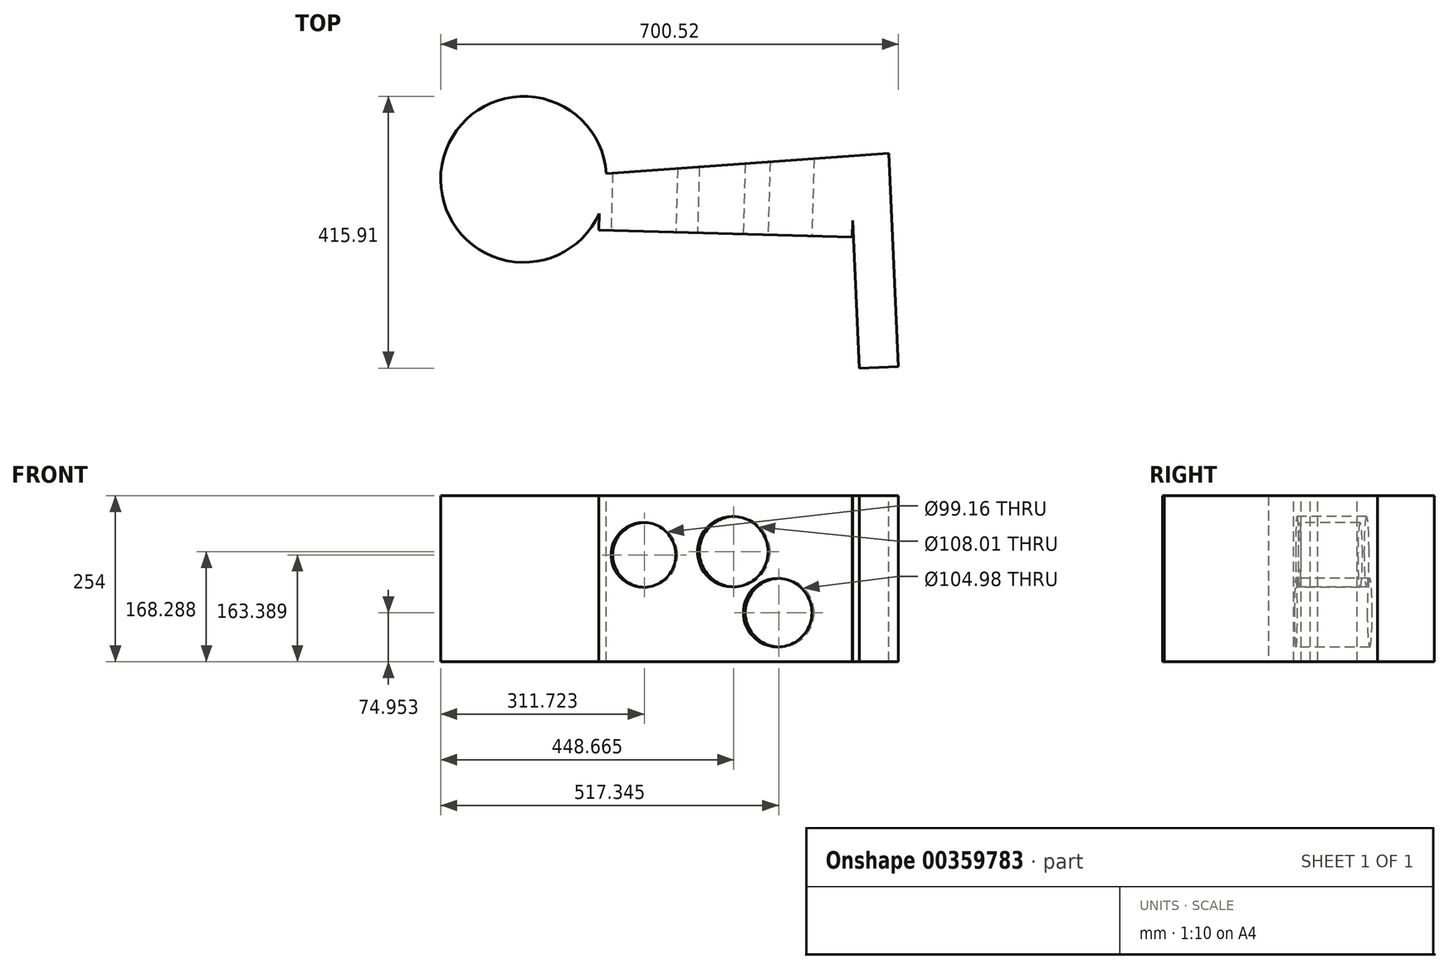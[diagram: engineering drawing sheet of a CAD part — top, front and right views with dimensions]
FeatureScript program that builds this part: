
annotation { "Feature Type Name" : "Feature", "Feature Type Description" : "" }
export const myFeature = defineFeature(function(context is Context, id is Id, definition is map)
    precondition{}
    {
        {
            var Q0;
            Q0=qCreatedBy(makeId("Top.planeOp"),FACE);
            var sketch = newSketch(context, id + "F0", { "sketchPlane" : qUnion([Q0])});
            skCircle(sketch, "E0", {"center": v(0, 0) * mm, "radius": 127 * mm});
            skSolve(sketch);
        }
        {
            var Q0;
            Q0=makeQuery(id+"F0.imprint","IMPRINT",FACE,{"disambiguationData":[TD([[makeQuery(id+"F0.imprint","IMPRINT",EDGE,{"derivedFrom":sQuery(id+"F0.wireOp",EDGE,"E0")}),1.0]])]});
            extrude(context, id + "F1", {"entities" : qUnion([Q0]), "depth" : 254 * mm});
        }
        {
            var Q0;
            Q0=makeQuery(id+"F1.opExtrude","CAP_FACE",FACE,{"disambiguationData":[OSD([sQuery(id+"F0.wireOp",EDGE,"E0")])],"isStart":false});
            var sketch = newSketch(context, id + "F2", { "sketchPlane" : qUnion([Q0])});
            skLineSegment(sketch, "E1", {"start": v(0, 0) * mm, "end": v(559.2, 39.98) * mm});
            skLineSegment(sketch, "E2", {"start": v(559.2, 39.98) * mm, "end": v(573.52, -286.29) * mm});
            skLineSegment(sketch, "E3", {"start": v(573.52, -286.29) * mm, "end": v(513.78, -288.91) * mm});
            skLineSegment(sketch, "E4", {"start": v(513.78, -288.91) * mm, "end": v(503.86, -62.83) * mm});
            skLineSegment(sketch, "E5", {"start": v(503.86, -62.83) * mm, "end": v(115.93, -51.87) * mm});
            skSolve(sketch);
        }
        {
            var Q0;
            {var subQ0=sQuery(id+"F2.wireOp",EDGE,"E2");Q0=makeQuery(id+"F2.imprint","IMPRINT",FACE,{"disambiguationData":[TD([[makeQuery(id+"F2.imprint","IMPRINT",EDGE,{"derivedFrom":subQ0}),-1.0]])]});}
            extrude(context, id + "F3", {"entities" : qUnion([Q0]), "operationType" : NewBodyOperationType.ADD, "oppositeDirection" : true, "depth" : 254 * mm});
        }
        {
            var Q0;
            Q0=makeQuery(id+"F3.opExtrude","SWEPT_FACE",FACE,{"disambiguationData":[OSD([sQuery(id+"F2.wireOp",EDGE,"E5")])]});
            extrude(context, id + "F4", {"entities" : qUnion([Q0]), "operationType" : NewBodyOperationType.ADD, "depth" : 25.4 * mm});
        }
        {
            var Q0;
            Q0=makeQuery(id+"F4.opExtrude","CAP_FACE",FACE,{"disambiguationData":[OSD([sQuery(id+"F2.wireOp",EDGE,"E5")])],"isStart":false});
            var sketch = newSketch(context, id + "F5", { "sketchPlane" : qUnion([Q0])});
            skCircle(sketch, "E6", {"center": v(185.52, 163.39) * mm, "radius": 49.58 * mm});
            skCircle(sketch, "E7", {"center": v(337.48, 190) * mm, "radius": 46.3 * mm});
            skCircle(sketch, "E8", {"center": v(387.78, 87.17) * mm, "radius": 39.13 * mm});
            skSolve(sketch);
        }
        {
            var Q0;
            Q0=makeQuery(id+"F5.imprint","IMPRINT",FACE,{"disambiguationData":[TD([[makeQuery(id+"F5.imprint","IMPRINT",EDGE,{"derivedFrom":sQuery(id+"F5.wireOp",EDGE,"E6")}),1.0]])]});
            extrude(context, id + "F6", {"entities" : qUnion([Q0]), "operationType" : NewBodyOperationType.REMOVE, "oppositeDirection" : true, "depth" : 210.82 * mm});
        }
        {
            var Q0;
            Q0=makeQuery(id+"F4.opExtrude","CAP_FACE",FACE,{"disambiguationData":[OSD([sQuery(id+"F2.wireOp",EDGE,"E5")])],"isStart":false});
            var sketch = newSketch(context, id + "F7", { "sketchPlane" : qUnion([Q0])});
            skCircle(sketch, "E9", {"center": v(322.32, 168.29) * mm, "radius": 54 * mm});
            skSolve(sketch);
        }
        {
            var Q0;
            Q0=makeQuery(id+"F7.imprint","IMPRINT",FACE,{"disambiguationData":[TD([[makeQuery(id+"F7.imprint","IMPRINT",EDGE,{"derivedFrom":sQuery(id+"F7.wireOp",EDGE,"E9")}),1.0]])]});
            extrude(context, id + "F8", {"entities" : qUnion([Q0]), "operationType" : NewBodyOperationType.REMOVE, "oppositeDirection" : true, "depth" : 254 * mm});
        }
        {
            var Q0;
            Q0=makeQuery(id+"F4.opExtrude","CAP_FACE",FACE,{"disambiguationData":[OSD([sQuery(id+"F2.wireOp",EDGE,"E5")])],"isStart":false});
            var sketch = newSketch(context, id + "F9", { "sketchPlane" : qUnion([Q0])});
            skCircle(sketch, "E10", {"center": v(390.93, 74.95) * mm, "radius": 52.5 * mm});
            skSolve(sketch);
        }
        {
            var Q0;
            Q0=makeQuery(id+"F9.imprint","IMPRINT",FACE,{"disambiguationData":[TD([[makeQuery(id+"F9.imprint","IMPRINT",EDGE,{"derivedFrom":sQuery(id+"F9.wireOp",EDGE,"E10")}),1.0]])]});
            extrude(context, id + "F10", {"entities" : qUnion([Q0]), "operationType" : NewBodyOperationType.REMOVE, "oppositeDirection" : true, "depth" : 254 * mm});
        }
    });
